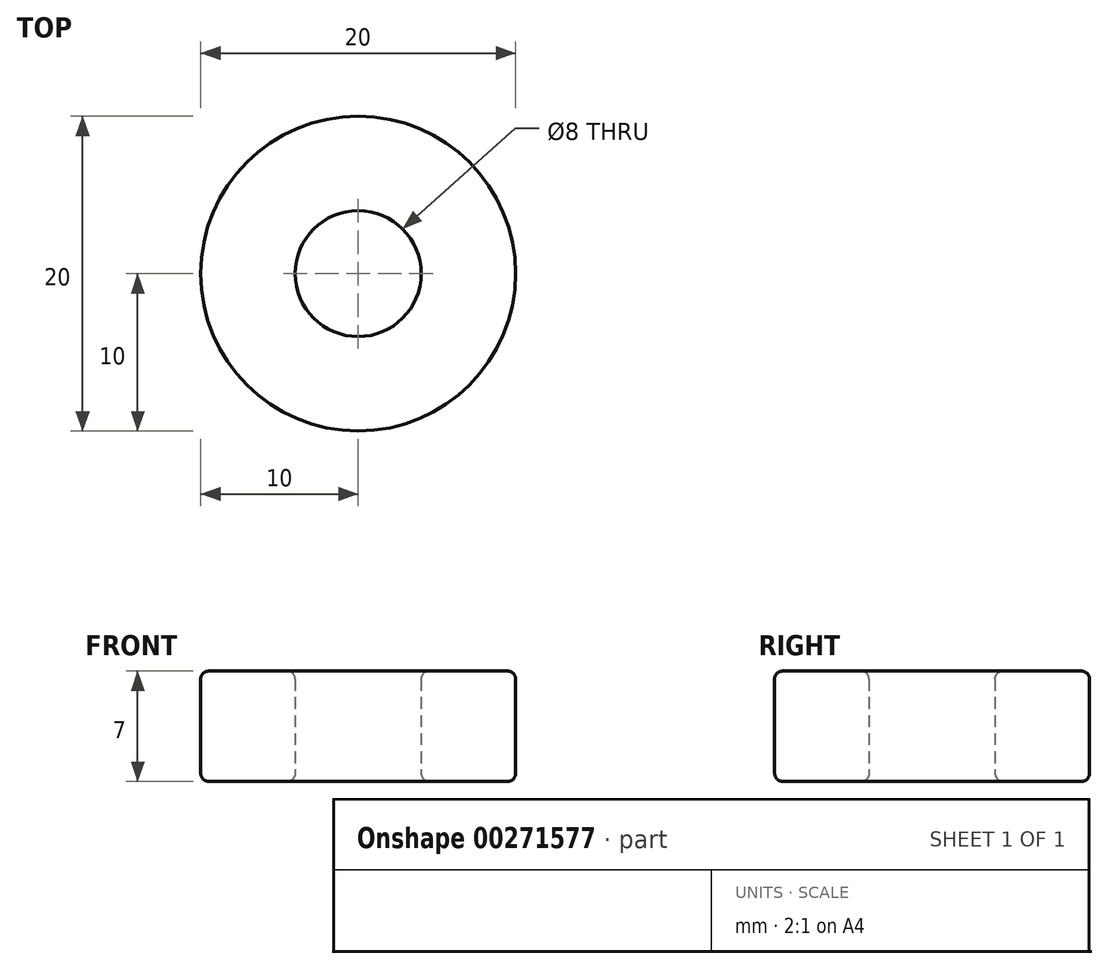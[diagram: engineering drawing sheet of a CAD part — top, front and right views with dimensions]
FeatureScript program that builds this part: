
annotation { "Feature Type Name" : "Feature", "Feature Type Description" : "" }
export const myFeature = defineFeature(function(context is Context, id is Id, definition is map)
    precondition{}
    {
        {
            var Q0;
            Q0=qCreatedBy(makeId("Top.planeOp"),FACE);
            var sketch = newSketch(context, id + "F0", { "sketchPlane" : qUnion([Q0])});
            skCircle(sketch, "E0", {"center": v(0, 0) * mm, "radius": 4 * mm});
            skCircle(sketch, "E1", {"center": v(0, 0) * mm, "radius": 10 * mm});
            skSolve(sketch);
        }
        {
            var Q0;
            Q0=makeQuery(id+"F0.imprint","IMPRINT",FACE,{"disambiguationData":[TD([[makeQuery(id+"F0.imprint","IMPRINT",EDGE,{"derivedFrom":sQuery(id+"F0.wireOp",EDGE,"E0")}),-1.0]])]});
            extrude(context, id + "F1", {"entities" : qUnion([Q0]), "depth" : 7 * mm});
        }
        {
            var Q0;
            Q0=makeQuery(id+"F1.opExtrude","CAP_FACE",FACE,{"disambiguationData":[OSD([sQuery(id+"F0.wireOp",EDGE,"E0"),sQuery(id+"F0.wireOp",EDGE,"E1")])],"isStart":false});
            var Q1;
            Q1=makeQuery(id+"F1.opExtrude","CAP_FACE",FACE,{"disambiguationData":[OSD([sQuery(id+"F0.wireOp",EDGE,"E0"),sQuery(id+"F0.wireOp",EDGE,"E1")])],"isStart":true});
            fillet(context, id + "F2", {"entities" : qUnion([Q0, Q1]), "radius" : .5 * mm, "tangentPropagation" : true, "allowEdgeOverflow" : false});
        }
    });
